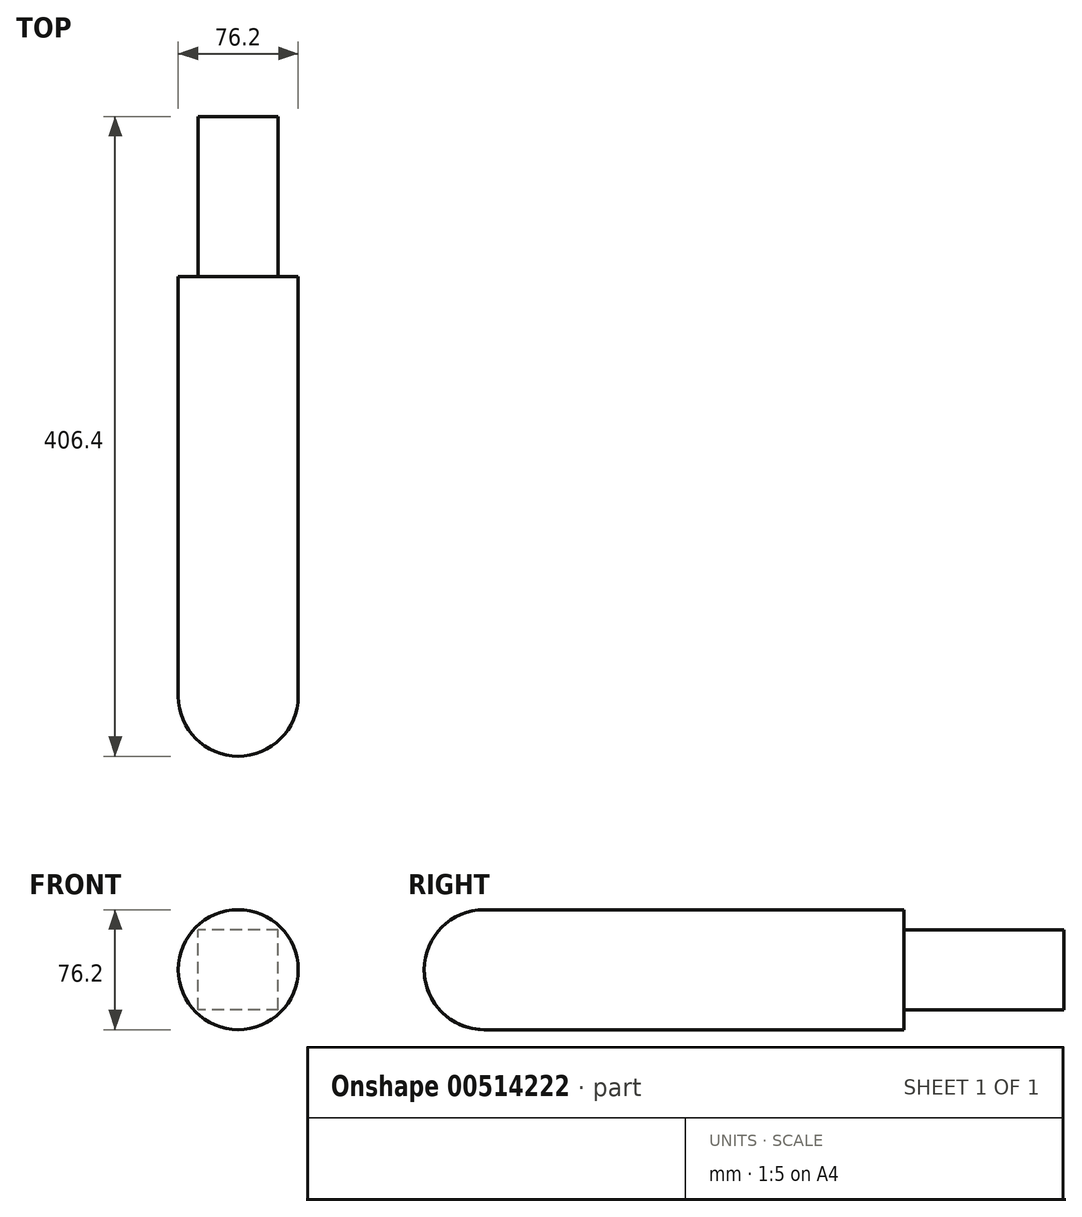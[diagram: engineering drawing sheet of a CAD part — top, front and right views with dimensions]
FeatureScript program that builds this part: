
annotation { "Feature Type Name" : "Feature", "Feature Type Description" : "" }
export const myFeature = defineFeature(function(context is Context, id is Id, definition is map)
    precondition{}
    {
        {
            var Q0;
            Q0=qCreatedBy(makeId("Front.planeOp"),FACE);
            var sketch = newSketch(context, id + "F0", { "sketchPlane" : qUnion([Q0])});
            skLineSegment(sketch, "E0.bottom", {"start": v(25.4, -25.4) * mm, "end": v(-25.4, -25.4) * mm});
            skLineSegment(sketch, "E0.top", {"start": v(25.4, 25.4) * mm, "end": v(-25.4, 25.4) * mm});
            skLineSegment(sketch, "E0.left", {"start": v(25.4, -25.4) * mm, "end": v(25.4, 25.4) * mm});
            skLineSegment(sketch, "E0.right", {"start": v(-25.4, -25.4) * mm, "end": v(-25.4, 25.4) * mm});
            skPoint(sketch, "E0.middle", {"position": v(0, 0) * mm});
            skSolve(sketch);
        }
        {
            var Q0;
            Q0 = qSketchRegion(id + "F0", true);
            extrude(context, id + "F1", {"entities" : qUnion([Q0]), "depth" : 101.6 * mm, "offsetDistance" : 25.4 * mm});
        }
        {
            var Q0;
            Q0=makeQuery(id+"F1.opExtrude","CAP_FACE",FACE,{"disambiguationData":[OSD([sQuery(id+"F0.wireOp",EDGE,"E0.bottom"),sQuery(id+"F0.wireOp",EDGE,"E0.top"),sQuery(id+"F0.wireOp",EDGE,"E0.left"),sQuery(id+"F0.wireOp",EDGE,"E0.right")])],"isStart":false});
            var sketch = newSketch(context, id + "F2", { "sketchPlane" : qUnion([Q0])});
            skCircle(sketch, "E1", {"center": v(0, 0) * mm, "radius": 38.1 * mm});
            skSolve(sketch);
        }
        {
            var Q0;
            Q0=makeQuery(id+"F2.imprint","IMPRINT",FACE,{"disambiguationData":[TD([[makeQuery(id+"F2.imprint","IMPRINT",EDGE,{"derivedFrom":sQuery(id+"F2.wireOp",EDGE,"E1")}),1.0]])]});
            var Q1;
            Q1=makeQuery(id+"F2.imprint","IMPRINT",FACE,{"disambiguationData":[TD([[makeQuery(id+"F2.imprint","IMPRINT",EDGE,{"derivedFrom":makeQuery(id+"F1.opExtrude","CAP_EDGE",EDGE,{"disambiguationData":[OSD([sQuery(id+"F0.wireOp",EDGE,"E0.bottom")])],"isStart":false})}),-1.0]])]});
            extrude(context, id + "F3", {"entities" : qUnion([Q0, Q1]), "operationType" : NewBodyOperationType.ADD, "depth" : 304.8 * mm, "offsetDistance" : 25.4 * mm});
        }
        {
            var Q0;
            Q0=makeQuery(id+"F3.opExtrude","CAP_EDGE",EDGE,{"disambiguationData":[OSD([sQuery(id+"F2.wireOp",EDGE,"E1")])],"isStart":false});
            fillet(context, id + "F4", {"entities" : qUnion([Q0]), "radius" : 38.1 * mm, "tangentPropagation" : true, "allowEdgeOverflow" : false});
        }
    });
